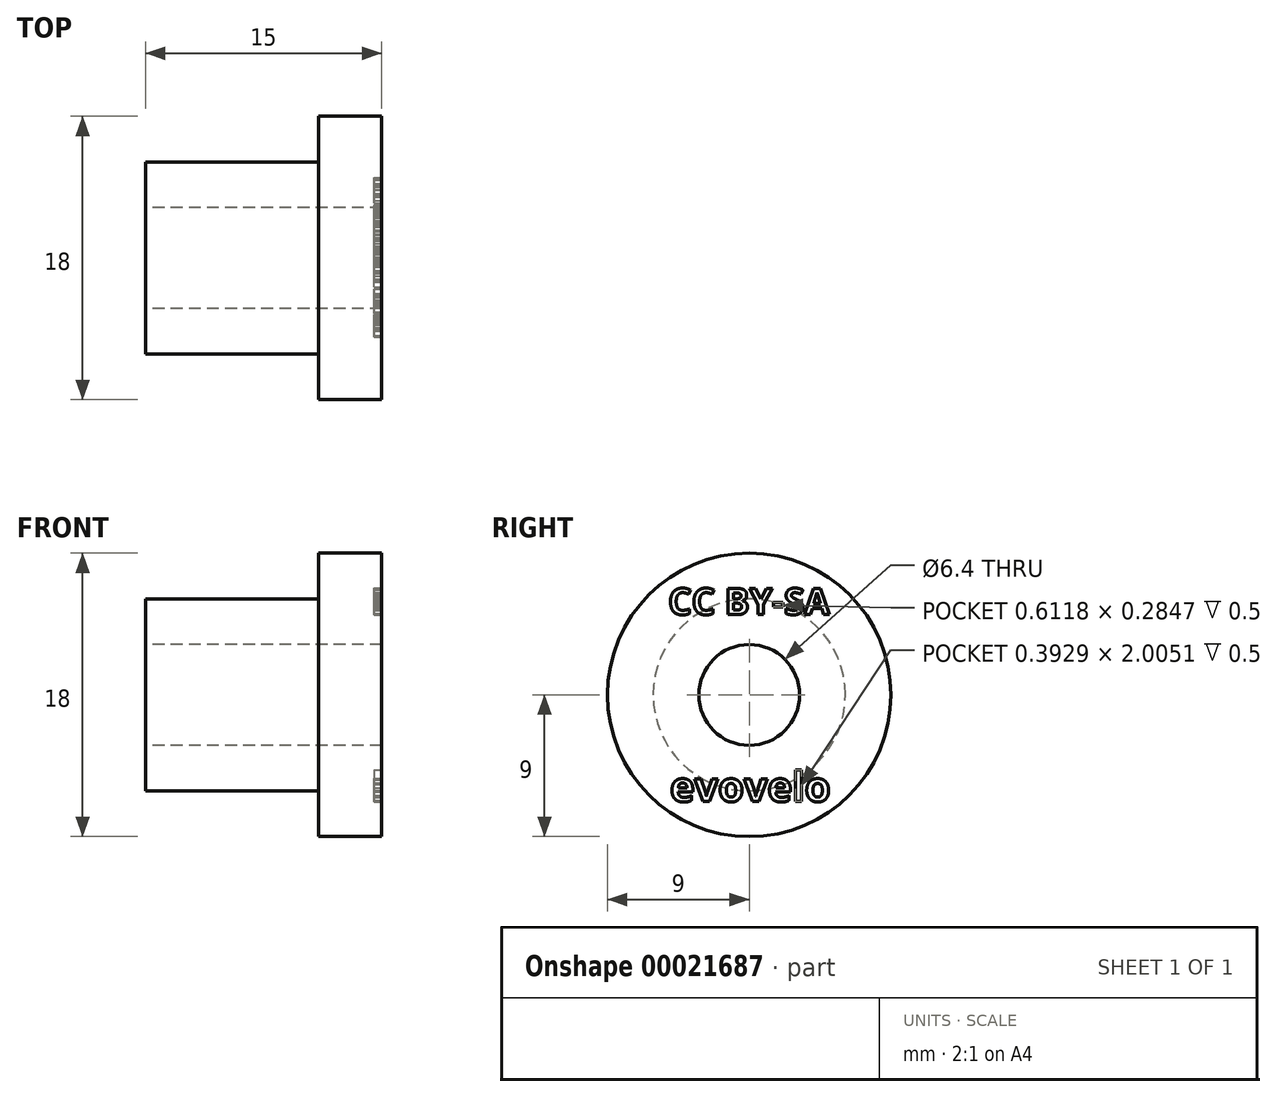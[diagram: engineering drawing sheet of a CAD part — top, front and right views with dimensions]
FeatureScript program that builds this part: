
annotation { "Feature Type Name" : "Feature", "Feature Type Description" : "" }
export const myFeature = defineFeature(function(context is Context, id is Id, definition is map)
    precondition{}
    {
        {
            var Q0;
            Q0=qCreatedBy(makeId("Top.planeOp"),FACE);
            var sketch = newSketch(context, id + "F0", { "sketchPlane" : qUnion([Q0])});
            skLineSegment(sketch, "E0", {"start": v(-3.9, 0) * mm, "end": v(29.57, 0) * mm, "construction": true});
            skLineSegment(sketch, "E1", {"start": v(0, 0) * mm, "end": v(0, 6.1) * mm});
            skLineSegment(sketch, "E2", {"start": v(0, 6.1) * mm, "end": v(11, 6.1) * mm});
            skLineSegment(sketch, "E3", {"start": v(11, 6.1) * mm, "end": v(11, 9) * mm});
            skLineSegment(sketch, "E4", {"start": v(11, 9) * mm, "end": v(15, 9) * mm});
            skLineSegment(sketch, "E5", {"start": v(15, 9) * mm, "end": v(15, 0) * mm});
            skLineSegment(sketch, "E6", {"start": v(15, 0) * mm, "end": v(0, 0) * mm});
            skSolve(sketch);
        }
        {
            var Q0;
            Q0=qSketchRegion(id+"F0",true);
            var Q1;
            Q1=sQuery(id+"F0.wireOp",EDGE,"E0");
            revolve(context, id + "F1", {"entities" : qUnion([Q0]), "axis" : qUnion([Q1]), "revolveType" : RevolveType.FULL});
        }
        {
            var Q0;
            Q0=makeQuery(id+"F1.opRevolve","SWEPT_FACE",FACE,{"disambiguationData":[OSD([sQuery(id+"F0.wireOp",EDGE,"E5")])]});
            var sketch = newSketch(context, id + "F2", { "sketchPlane" : qUnion([Q0])});
            skPoint(sketch, "E7", {"position": v(0, 0) * mm});
            skText(sketch, "E8", { "text": "CC BY-SA", "fontName": "OpenSans-Bold.ttf"});
            skText(sketch, "E9", { "text": "evovelo", "fontName": "OpenSans-Bold.ttf"});
            const initialGuessF2  = {"E8": [-0.00514, 0.0051, 1, 0, 0.00168], "E9": [-0.00503, -0.00678, 1, 0, 0.0019]};
            skSetInitialGuess(sketch, initialGuessF2);
            skSolve(sketch);
        }
        {
            var Q0;
            Q0=sQuery(id+"F2.wireOp",VERTEX,"E7");
            var Q1;
            Q1=makeQuery(id+"F1.opRevolve","SWEPT_BODY",BODY,{"disambiguationData":[OSD([sQuery(id+"F0.wireOp",EDGE,"E1"),sQuery(id+"F0.wireOp",EDGE,"E2"),sQuery(id+"F0.wireOp",EDGE,"E3"),sQuery(id+"F0.wireOp",EDGE,"E4"),sQuery(id+"F0.wireOp",EDGE,"E5"),sQuery(id+"F0.wireOp",EDGE,"E6")])]});
            hole(context, id + "F3", {"style" : HoleStyle.SIMPLE, "holeDiameter" : 6.4 * mm, "endStyle" : HoleEndStyle.BLIND, "holeDepth" : 15 * mm, "locations" : qUnion([Q0]), "scope" : qUnion([Q1])});
        }
        {
            var Q0;
            Q0=qSketchRegion(id+"F2",true);
            extrude(context, id + "F4", {"entities" : qUnion([Q0]), "operationType" : NewBodyOperationType.REMOVE, "oppositeDirection" : true, "depth" : 0.5 * mm});
        }
    });
